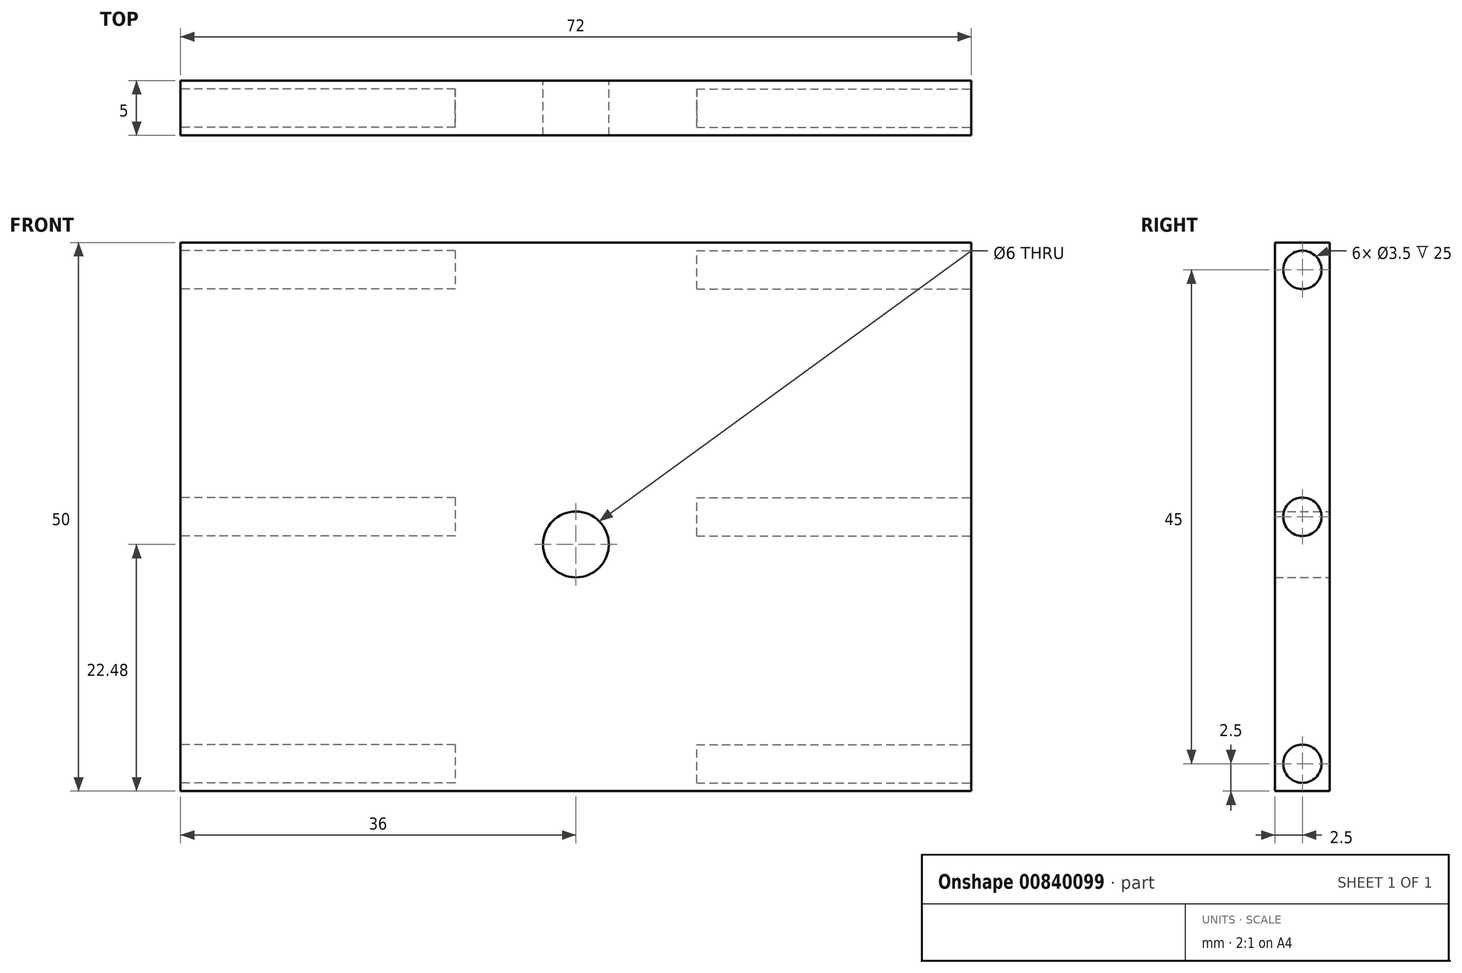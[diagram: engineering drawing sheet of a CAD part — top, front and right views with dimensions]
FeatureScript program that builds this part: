
annotation { "Feature Type Name" : "Feature", "Feature Type Description" : "" }
export const myFeature = defineFeature(function(context is Context, id is Id, definition is map)
    precondition{}
    {
        {
            var Q0;
            Q0=qCreatedBy(makeId("Front.planeOp"),FACE);
            var sketch = newSketch(context, id + "F0", { "sketchPlane" : qUnion([Q0])});
            skLineSegment(sketch, "E0.bottom", {"start": v(36, -25) * mm, "end": v(-36, -25) * mm});
            skLineSegment(sketch, "E0.top", {"start": v(36, 25) * mm, "end": v(-36, 25) * mm});
            skLineSegment(sketch, "E0.left", {"start": v(36, -25) * mm, "end": v(36, 25) * mm});
            skLineSegment(sketch, "E0.right", {"start": v(-36, -25) * mm, "end": v(-36, 25) * mm});
            skPoint(sketch, "E0.middle", {"position": v(0, 0) * mm});
            skCircle(sketch, "E1", {"center": v(0, -2.52) * mm, "radius": 3 * mm});
            skPoint(sketch, "E1.centerSnap0", {"position": v(0, 25) * mm});
            skSolve(sketch);
        }
        {
            var Q0;
            Q0 = qSketchRegion(id + "F0", true);
            extrude(context, id + "F1", {"entities" : qUnion([Q0]), "depth" : 5 * mm, "offsetDistance" : 25 * mm});
        }
        {
            var Q0;
            Q0=makeQuery(id+"F1.opExtrude","SWEPT_FACE",FACE,{"disambiguationData":[OSD([sQuery(id+"F0.wireOp",EDGE,"E0.right")])]});
            var sketch = newSketch(context, id + "F2", { "sketchPlane" : qUnion([Q0])});
            skCircle(sketch, "E2", {"center": v(2.5, 22.5) * mm, "radius": 1.75 * mm});
            skPoint(sketch, "E2.centerSnap0", {"position": v(2.5, 25) * mm});
            skCircle(sketch, "E3", {"center": v(2.5, -22.5) * mm, "radius": 1.75 * mm});
            skPoint(sketch, "E3.centerSnap0", {"position": v(2.5, -25) * mm});
            skCircle(sketch, "E4", {"center": v(2.5, 0) * mm, "radius": 1.75 * mm});
            skSolve(sketch);
        }
        {
            var Q0;
            Q0 = qSketchRegion(id + "F2", true);
            extrude(context, id + "F3", {"entities" : qUnion([Q0]), "operationType" : NewBodyOperationType.REMOVE, "oppositeDirection" : true, "depth" : 25 * mm, "offsetDistance" : 25 * mm});
        }
        {
            var Q0;
            Q0=makeQuery(id+"F1.opExtrude","SWEPT_FACE",FACE,{"disambiguationData":[OSD([sQuery(id+"F0.wireOp",EDGE,"E0.left")])]});
            var sketch = newSketch(context, id + "F4", { "sketchPlane" : qUnion([Q0])});
            skPoint(sketch, "E5.centerSnap0", {"position": v(-2.5, 25) * mm});
            skPoint(sketch, "E6.centerSnap0", {"position": v(-2.5, -25) * mm});
            skCircle(sketch, "E7", {"center": v(-2.5, 0) * mm, "radius": 1.75 * mm});
            skCircle(sketch, "E8", {"center": v(-2.5, 22.5) * mm, "radius": 1.75 * mm});
            skCircle(sketch, "E9", {"center": v(-2.5, -22.5) * mm, "radius": 1.75 * mm});
            skSolve(sketch);
        }
        {
            var Q0;
            Q0 = qSketchRegion(id + "F4", true);
            extrude(context, id + "F5", {"entities" : qUnion([Q0]), "operationType" : NewBodyOperationType.REMOVE, "oppositeDirection" : true, "depth" : 25 * mm, "offsetDistance" : 25 * mm});
        }
    });
